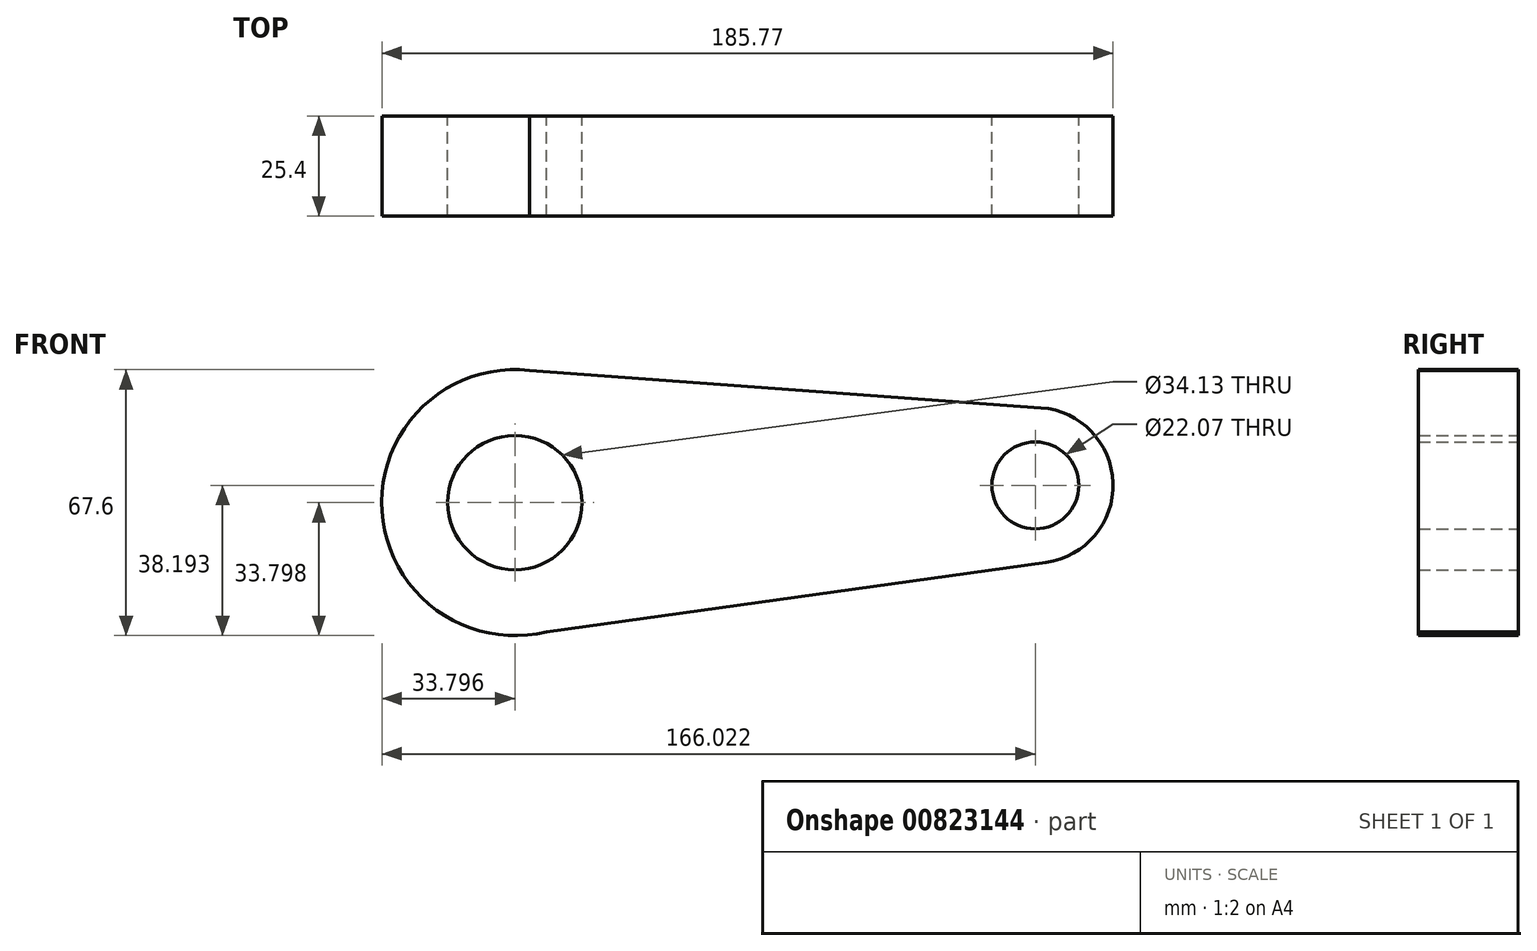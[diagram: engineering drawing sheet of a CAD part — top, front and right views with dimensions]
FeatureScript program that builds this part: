
annotation { "Feature Type Name" : "Feature", "Feature Type Description" : "" }
export const myFeature = defineFeature(function(context is Context, id is Id, definition is map)
    precondition{}
    {
        {
            var Q0;
            Q0=qCreatedBy(makeId("Front.planeOp"),FACE);
            var sketch = newSketch(context, id + "F0", { "sketchPlane" : qUnion([Q0])});
            skCircle(sketch, "E0", {"center": v(-49.52, 43.74) * mm, "radius": 17.06 * mm});
            skArc(sketch, "E1", {"start": v(-45.76, 77.33) * mm, "mid": v(-83.25, 41.53) * mm, "end": v(-41.42, 10.93) * mm});
            skCircle(sketch, "E2", {"center": v(82.7, 48.13) * mm, "radius": 11.03 * mm});
            skArc(sketch, "E3", {"start": v(85.42, 28.57) * mm, "mid": v(102.44, 48.78) * mm, "end": v(84.14, 67.83) * mm});
            skLineSegment(sketch, "E4", {"start": v(-45.76, 77.33) * mm, "end": v(84.14, 67.83) * mm});
            skLineSegment(sketch, "E5", {"start": v(-41.42, 10.93) * mm, "end": v(85.42, 28.57) * mm});
            skSolve(sketch);
        }
        {
            var Q0;
            Q0=makeQuery(id+"F0.imprint","IMPRINT",FACE,{"disambiguationData":[TD([[makeQuery(id+"F0.imprint","IMPRINT",EDGE,{"derivedFrom":sQuery(id+"F0.wireOp",EDGE,"E0")}),-1.0]])]});
            extrude(context, id + "F1", {"entities" : qUnion([Q0]), "depth" : 25.4 * mm, "offsetDistance" : 25.4 * mm});
        }
    });
